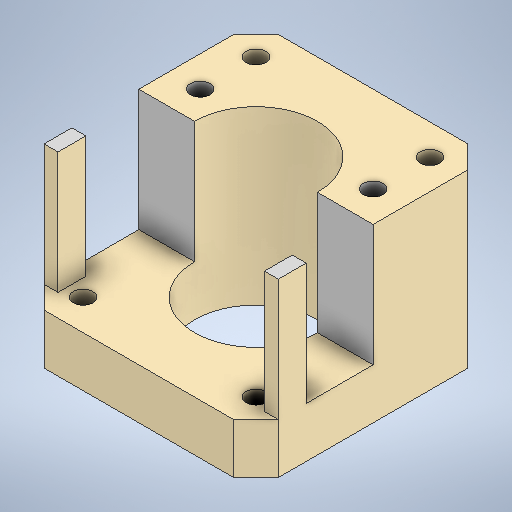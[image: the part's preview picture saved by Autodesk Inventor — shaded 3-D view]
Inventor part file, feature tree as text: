
AUTODESK INVENTOR PART (.ipt)
format: ipt  version: 2025 (Build 290162000, 162)  size: 336,384 bytes
history: native  units: in
note: dims shown in document units (in); Inventor stores cm internally (conversion verified against a paired STEP export)
features: sketch x6, extrude x4, chamfer x3, other x2
ambient origin geometry x8: Origin, YZ Plane, XZ Plane, XY Plane, X Axis, Y Axis, Z Axis, Center Point
bodies: Solid1 (feature_tree)
feature tree (15):
  extrude  "Extrusion1"  Depth=1.6535in
  sketch  "Sketch2"  dims[d3=0.7874in d5=1.2205in d6=0.7874in d8=1.2205in]
  chamfer  "Chamfer1"  Distance=0.3543in
  extrude  "Extrusion2"  Depth=0.1575in TaperAngle=45.0deg
  chamfer  "Chamfer5"  Distance=0.1575in
  chamfer  "Chamfer6"  Distance=0.0984in
  extrude  "Extrusion3"  Depth=0.4724in
  extrude  "Extrusion4"  Depth=0.4724in
  sketch  "Sketch1"  dims[d0=1.6535in d1=1.6535in]
  sketch  "Sketch Rectangular Pattern1"  dims[d2=0.1378in]
  sketch  "Sketch3"  dims[d12=0.2165in]
  sketch  "Sketch4"  dims[d13=0.8661in d14=0.3543in d15=0.0in d16=0.1575in d17=0.0787in d18=45.0deg d19=0.1575in d20=0.0984in d22=0.4724in d23=0.1575in d24=0.4724in d25=0.0984in d26=0.8583in d27=0.0in d34=0.1969in d36=0.1969in d37=0.1575in d42=0.1575in d43=0.0787in d44=45.0deg d45=0.1575in d46=0.0787in d47=45.0deg d48=0.1378in d49=0.3937in d50=0.1378in d51=0.3937in d52=1.2126in d53=0.0in d55=0.225in d56=0.0in d57=0.7874in d59=1.2205in d60=0.3937in d62=0.3937in d64=0.9764in d65=0.0in]
  sketch  "Sketch Rectangular Pattern2"  dims[d11=0.2165in]
  other  "Finish1"
  other  "Finish2"
